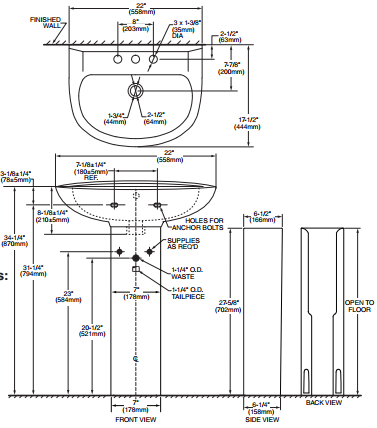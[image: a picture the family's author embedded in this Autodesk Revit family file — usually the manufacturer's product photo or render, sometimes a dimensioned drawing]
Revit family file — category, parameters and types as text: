
# Revit family: Basin-Pedestal-American_Standard-Evolution-0467_Series
name_source: partatom
category: Plumbing Fixtures
revit_build: Autodesk Revit 2014 (Build: 20130308_1515(x64)
units: mm (PartAtom-declared; Revit-internal decimal feet)

## types (3) — shared parameters
Assembly Code = D2010310
Basin Shape = D Shape
CW Connection = Yes
CWFU = 1.5
Cold Water Connection Diameter = 3/8"
Cold Water Connection Height = 23"
Cold Water Connection Radius = 3/16"
Cold Water Connection Width = 4"
Default Elevation = 34"
HW Connection = Yes
HWFU = 1.5
Height = 8 1/8"
Hot Water Connection Diameter = 0"
Hot Water Connection Height = 23"
Hot Water Connection Radius = 3/16"
Hot Water Connection Width = 4"
Installation Type = Pedestal
Length = 17 1/2"
Manufacturer = American Standard
Material = Vitreous China-American Standard-020-White
Pedestal Option = Yes
Price = Prices may vary. Please consult Manufacturer Representative for most up-to-date price list.
Product Documentation Link = https://www.americanstandard-us.com
Product Page URL = https://www.americanstandard-us.com
URL = https://www.americanstandard-us.com
Vent Connection = No
WFU = 2
Waste Connection = Yes
Waste Connection Diameter = 1 1/4"
Waste Connection Height = 21"
Waste Connection Radius = 5/8"
Width = 22"

## per-type parameters (varying)
| type | Description | Hole Punch Location |
| 0467.400 | Evolution 22" pedestal sink. Basin only. 4" centers. | 4" |
| 0467.800 | Evolution 22" pedestal sink. Basin only. 8" centers. | 8" |
| 0467.100 | Evolution 22" pedestal sink. Basin only. Center hole only. | 50" |

note: column(s) folded — value = type name in every type: Model

## geometry (parser evidence)
native form markers: Sweep x1
no freeform markers — native parametric forms only
